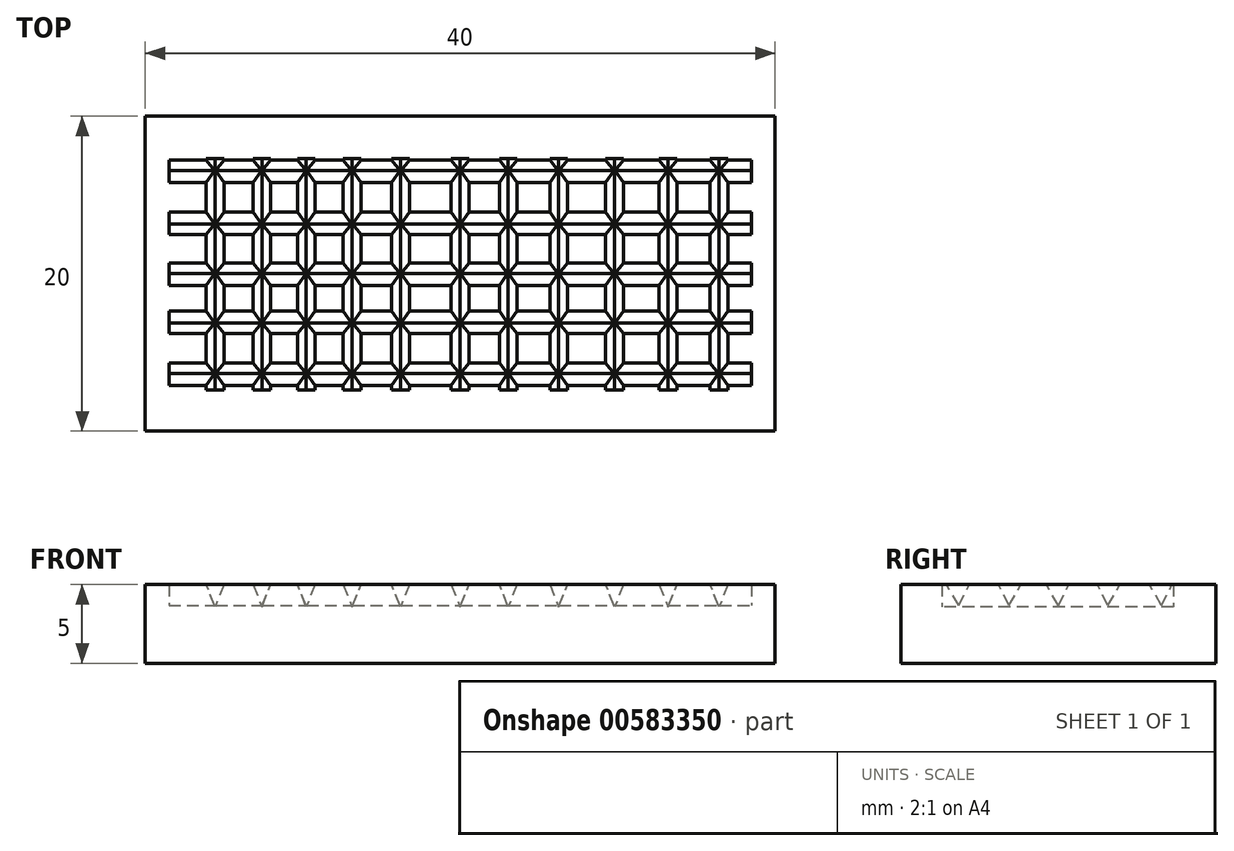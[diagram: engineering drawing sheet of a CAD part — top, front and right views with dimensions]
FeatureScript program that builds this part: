
annotation { "Feature Type Name" : "Feature", "Feature Type Description" : "" }
export const myFeature = defineFeature(function(context is Context, id is Id, definition is map)
    precondition{}
    {
        {
            var Q0;
            Q0=qCreatedBy(makeId("Top.planeOp"),FACE);
            var sketch = newSketch(context, id + "F0", { "sketchPlane" : qUnion([Q0])});
            skLineSegment(sketch, "E0.bottom", {"start": v(-20, 10) * mm, "end": v(20, 10) * mm});
            skLineSegment(sketch, "E0.top", {"start": v(-20, -10) * mm, "end": v(20, -10) * mm});
            skLineSegment(sketch, "E0.left", {"start": v(-20, 10) * mm, "end": v(-20, -10) * mm});
            skLineSegment(sketch, "E0.right", {"start": v(20, 10) * mm, "end": v(20, -10) * mm});
            skPoint(sketch, "E0.middle", {"position": v(0, 0) * mm});
            skSolve(sketch);
        }
        {
            var Q0;
            Q0 = qSketchRegion(id + "F0", true);
            extrude(context, id + "F1", {"entities" : qUnion([Q0]), "depth" : 5 * mm, "offsetDistance" : 25 * mm});
        }
        {
            var Q0;
            Q0=qCreatedBy(makeId("Right.planeOp"),FACE);
            var sketch = newSketch(context, id + "F2", { "sketchPlane" : qUnion([Q0])});
            skLineSegment(sketch, "E1", {"start": v(-0.37, 5.18) * mm, "end": v(0.37, 5.18) * mm});
            skLineSegment(sketch, "E2", {"start": v(0.37, 5.18) * mm, "end": v(0.76, 5.18) * mm});
            skLineSegment(sketch, "E3", {"start": v(-0.37, 5.18) * mm, "end": v(-0.87, 5.18) * mm});
            skLineSegment(sketch, "E4", {"start": v(-0.87, 5.18) * mm, "end": v(0, 3.67) * mm});
            skLineSegment(sketch, "E5", {"start": v(0.76, 5.18) * mm, "end": v(0, 3.67) * mm});
            skLineSegment(sketch, "E6.MirrorCS", {"start": v(3.51, 5.18) * mm, "end": v(2.77, 5.18) * mm});
            skLineSegment(sketch, "E7.MirrorCS", {"start": v(3.51, 5.18) * mm, "end": v(4.01, 5.18) * mm});
            skLineSegment(sketch, "E8.MirrorCS", {"start": v(2.77, 5.18) * mm, "end": v(2.38, 5.18) * mm});
            skLineSegment(sketch, "E9.MirrorCS", {"start": v(2.38, 5.18) * mm, "end": v(3.14, 3.67) * mm});
            skLineSegment(sketch, "E10.MirrorCS", {"start": v(4.01, 5.18) * mm, "end": v(3.14, 3.67) * mm});
            skLineSegment(sketch, "E11.MirrorCS", {"start": v(7.3, 5.18) * mm, "end": v(6.55, 3.67) * mm});
            skLineSegment(sketch, "E12.MirrorCS", {"start": v(6.92, 5.18) * mm, "end": v(7.3, 5.18) * mm});
            skLineSegment(sketch, "E13.MirrorCS", {"start": v(6.18, 5.18) * mm, "end": v(6.92, 5.18) * mm});
            skLineSegment(sketch, "E14.MirrorCS", {"start": v(6.18, 5.18) * mm, "end": v(5.68, 5.18) * mm});
            skLineSegment(sketch, "E15", {"start": v(5.68, 5.18) * mm, "end": v(6.55, 3.67) * mm});
            skLineSegment(sketch, "E16.MirrorCS", {"start": v(-2.27, 5.18) * mm, "end": v(-3.14, 3.67) * mm});
            skLineSegment(sketch, "E17.MirrorCS", {"start": v(-2.77, 5.18) * mm, "end": v(-2.27, 5.18) * mm});
            skLineSegment(sketch, "E18.MirrorCS", {"start": v(-2.77, 5.18) * mm, "end": v(-3.51, 5.18) * mm});
            skLineSegment(sketch, "E19.MirrorCS", {"start": v(-3.51, 5.18) * mm, "end": v(-3.9, 5.18) * mm});
            skLineSegment(sketch, "E20.MirrorCS", {"start": v(-3.9, 5.18) * mm, "end": v(-3.14, 3.67) * mm});
            skPoint(sketch, "E21.MirrorCS.end.orphan", {"position": v(-1.57, -0.47) * mm});
            skPoint(sketch, "E21.MirrorCS.start.orphan", {"position": v(-1.57, 5.59) * mm});
            skPoint(sketch, "E22.end.orphan", {"position": v(1.57, -0.47) * mm});
            skPoint(sketch, "E22.start.orphan", {"position": v(1.57, 5.59) * mm});
            skPoint(sketch, "E23.start.orphan", {"position": v(4.85, 5.18) * mm});
            skLineSegment(sketch, "E24.MirrorCS", {"start": v(-5.58, 5.18) * mm, "end": v(-6.34, 3.67) * mm});
            skLineSegment(sketch, "E25.MirrorCS", {"start": v(-5.96, 5.18) * mm, "end": v(-5.58, 5.18) * mm});
            skLineSegment(sketch, "E26.MirrorCS", {"start": v(-6.7, 5.18) * mm, "end": v(-5.96, 5.18) * mm});
            skLineSegment(sketch, "E27.MirrorCS", {"start": v(-6.7, 5.18) * mm, "end": v(-7.2, 5.18) * mm});
            skLineSegment(sketch, "E28.MirrorCS", {"start": v(-7.2, 5.18) * mm, "end": v(-6.34, 3.67) * mm});
            skSolve(sketch);
        }
        {
            var Q0;
            Q0 = qSketchRegion(id + "F2", true);
            extrude(context, id + "F3", {"entities" : qUnion([Q0]), "operationType" : NewBodyOperationType.REMOVE, "oppositeDirection" : true, "depth" : 18.5 * mm, "offsetDistance" : 25 * mm, "hasSecondDirection" : true, "secondDirectionOppositeDirection" : false, "secondDirectionDepth" : 18.5 * mm});
        }
        {
            var Q0;
            Q0=makeQuery(id+"F1.opExtrude","SWEPT_FACE",FACE,{"disambiguationData":[OSD([sQuery(id+"F0.wireOp",EDGE,"E0.top")])]});
            var sketch = newSketch(context, id + "F4", { "sketchPlane" : qUnion([Q0])});
            skPoint(sketch, "E29.startSnap0", {"position": v(0, 5) * mm});
            skLineSegment(sketch, "E30", {"start": v(0, 5.21) * mm, "end": v(-0.65, 5.21) * mm});
            skLineSegment(sketch, "E31", {"start": v(-0.65, 5.21) * mm, "end": v(0, 3.6) * mm});
            skLineSegment(sketch, "E32", {"start": v(0, 3.6) * mm, "end": v(0.65, 5.21) * mm});
            skLineSegment(sketch, "E33", {"start": v(0.65, 5.21) * mm, "end": v(0, 5.21) * mm});
            skPoint(sketch, "E29.start.orphan", {"position": v(0, 6) * mm});
            skLineSegment(sketch, "E34.MirrorCS", {"start": v(-3.14, 5.21) * mm, "end": v(-3.79, 3.6) * mm});
            skLineSegment(sketch, "E35.MirrorCS", {"start": v(-3.79, 5.21) * mm, "end": v(-3.14, 5.21) * mm});
            skLineSegment(sketch, "E36.MirrorCS", {"start": v(-4.44, 5.21) * mm, "end": v(-3.79, 5.21) * mm});
            skLineSegment(sketch, "E37.MirrorCS", {"start": v(-3.79, 3.6) * mm, "end": v(-4.44, 5.21) * mm});
            skLineSegment(sketch, "E38.MirrorCS", {"start": v(-6.86, 3.6) * mm, "end": v(-6.2, 5.21) * mm});
            skLineSegment(sketch, "E39.MirrorCS", {"start": v(-7.5, 5.21) * mm, "end": v(-6.86, 3.6) * mm});
            skLineSegment(sketch, "E40.MirrorCS", {"start": v(-6.86, 5.21) * mm, "end": v(-7.5, 5.21) * mm});
            skLineSegment(sketch, "E41.MirrorCS", {"start": v(-6.2, 5.21) * mm, "end": v(-6.86, 5.21) * mm});
            skLineSegment(sketch, "E42.MirrorCS", {"start": v(-9.12, 5.21) * mm, "end": v(-9.77, 3.6) * mm});
            skLineSegment(sketch, "E43.MirrorCS", {"start": v(-9.77, 3.6) * mm, "end": v(-10.42, 5.21) * mm});
            skLineSegment(sketch, "E44.MirrorCS", {"start": v(-10.42, 5.21) * mm, "end": v(-9.77, 5.21) * mm});
            skLineSegment(sketch, "E45.MirrorCS", {"start": v(-9.77, 5.21) * mm, "end": v(-9.12, 5.21) * mm});
            skLineSegment(sketch, "E46.MirrorCS", {"start": v(-12.6, 3.6) * mm, "end": v(-11.94, 5.21) * mm});
            skLineSegment(sketch, "E47.MirrorCS", {"start": v(-13.25, 5.21) * mm, "end": v(-12.6, 3.6) * mm});
            skLineSegment(sketch, "E48.MirrorCS", {"start": v(-12.6, 5.21) * mm, "end": v(-13.25, 5.21) * mm});
            skLineSegment(sketch, "E49.MirrorCS", {"start": v(-11.94, 5.21) * mm, "end": v(-12.6, 5.21) * mm});
            skLineSegment(sketch, "E50.MirrorCS", {"start": v(-14.9, 5.21) * mm, "end": v(-15.56, 3.6) * mm});
            skLineSegment(sketch, "E51.MirrorCS", {"start": v(-15.56, 3.6) * mm, "end": v(-16.21, 5.21) * mm});
            skLineSegment(sketch, "E52.MirrorCS", {"start": v(-16.21, 5.21) * mm, "end": v(-15.56, 5.21) * mm});
            skLineSegment(sketch, "E53.MirrorCS", {"start": v(-15.56, 5.21) * mm, "end": v(-14.9, 5.21) * mm});
            skLineSegment(sketch, "E54.MirrorCS", {"start": v(3.05, 3.6) * mm, "end": v(2.4, 5.21) * mm});
            skLineSegment(sketch, "E55.MirrorCS", {"start": v(3.7, 5.21) * mm, "end": v(3.05, 3.6) * mm});
            skLineSegment(sketch, "E56.MirrorCS", {"start": v(3.05, 5.21) * mm, "end": v(3.7, 5.21) * mm});
            skLineSegment(sketch, "E57.MirrorCS", {"start": v(2.4, 5.21) * mm, "end": v(3.05, 5.21) * mm});
            skLineSegment(sketch, "E58.MirrorCS", {"start": v(5.6, 5.21) * mm, "end": v(6.26, 3.6) * mm});
            skLineSegment(sketch, "E59.MirrorCS", {"start": v(6.26, 5.21) * mm, "end": v(5.6, 5.21) * mm});
            skLineSegment(sketch, "E60.MirrorCS", {"start": v(6.91, 5.21) * mm, "end": v(6.26, 5.21) * mm});
            skLineSegment(sketch, "E61.MirrorCS", {"start": v(6.26, 3.6) * mm, "end": v(6.91, 5.21) * mm});
            skLineSegment(sketch, "E62.MirrorCS", {"start": v(9.81, 3.6) * mm, "end": v(9.16, 5.21) * mm});
            skLineSegment(sketch, "E63.MirrorCS", {"start": v(9.16, 5.21) * mm, "end": v(9.81, 5.21) * mm});
            skLineSegment(sketch, "E64.MirrorCS", {"start": v(9.81, 5.21) * mm, "end": v(10.46, 5.21) * mm});
            skLineSegment(sketch, "E65.MirrorCS", {"start": v(10.46, 5.21) * mm, "end": v(9.81, 3.6) * mm});
            skLineSegment(sketch, "E66.MirrorCS", {"start": v(12.56, 5.21) * mm, "end": v(13.2, 3.6) * mm});
            skLineSegment(sketch, "E67.MirrorCS", {"start": v(13.2, 5.21) * mm, "end": v(12.56, 5.21) * mm});
            skLineSegment(sketch, "E68.MirrorCS", {"start": v(13.86, 5.21) * mm, "end": v(13.2, 5.21) * mm});
            skLineSegment(sketch, "E69.MirrorCS", {"start": v(13.2, 3.6) * mm, "end": v(13.86, 5.21) * mm});
            skLineSegment(sketch, "E70.MirrorCS", {"start": v(16.45, 3.6) * mm, "end": v(15.8, 5.21) * mm});
            skLineSegment(sketch, "E71.MirrorCS", {"start": v(15.8, 5.21) * mm, "end": v(16.45, 5.21) * mm});
            skLineSegment(sketch, "E72.MirrorCS", {"start": v(17.1, 5.21) * mm, "end": v(16.45, 3.6) * mm});
            skLineSegment(sketch, "E73.MirrorCS", {"start": v(16.45, 5.21) * mm, "end": v(17.1, 5.21) * mm});
            skPoint(sketch, "E74.start.orphan", {"position": v(-8.31, 5.21) * mm});
            skSolve(sketch);
        }
        {
            var Q0;
            Q0 = qSketchRegion(id + "F4", true);
            extrude(context, id + "F5", {"entities" : qUnion([Q0]), "operationType" : NewBodyOperationType.REMOVE, "oppositeDirection" : true, "depth" : 17.3 * mm, "offsetDistance" : 25 * mm, "hasSecondDirection" : true, "secondDirectionOppositeDirection" : true, "secondDirectionDepth" : 2.6 * mm});
        }
    });
